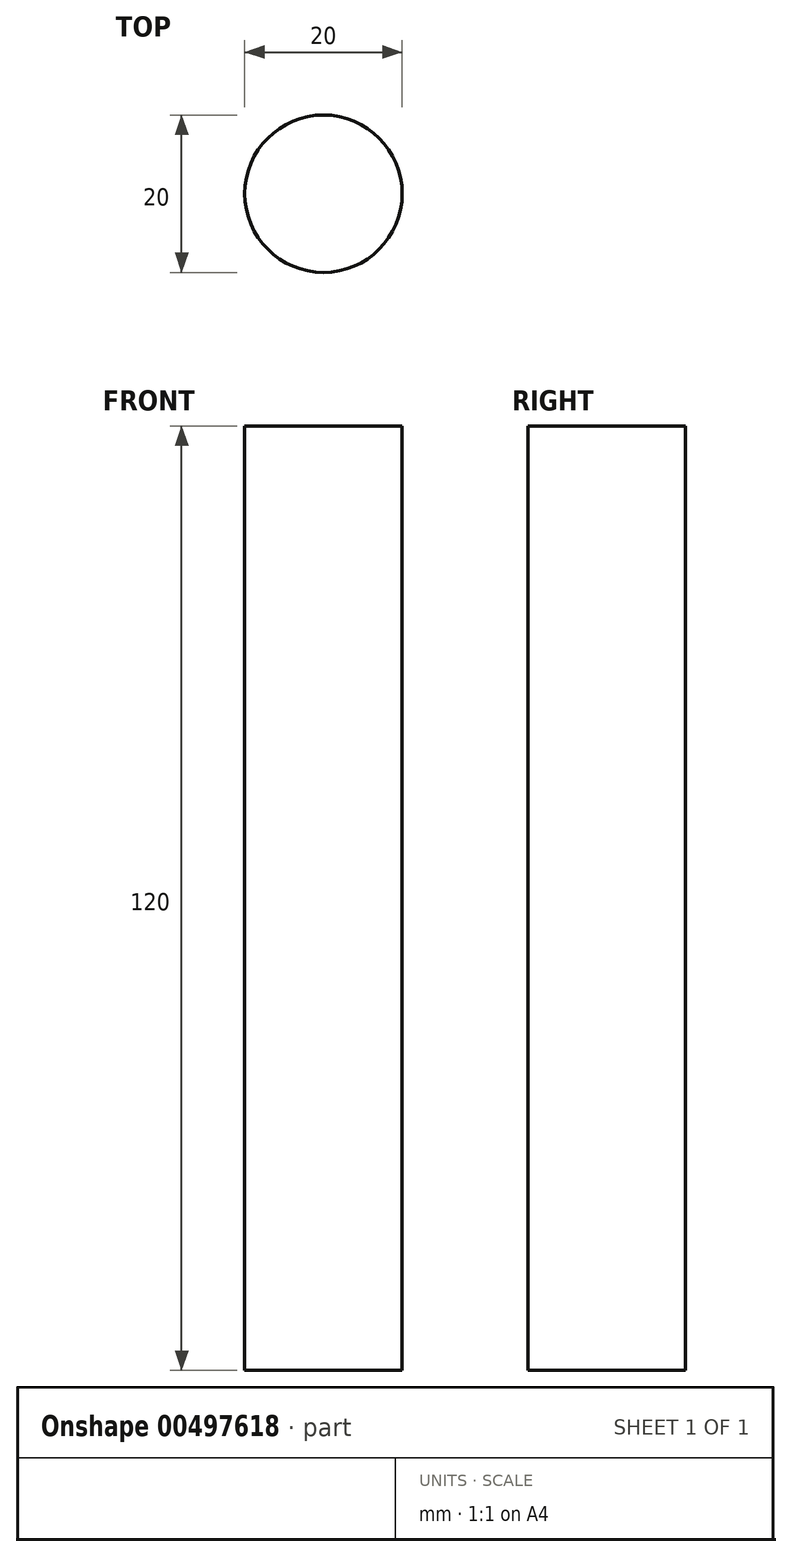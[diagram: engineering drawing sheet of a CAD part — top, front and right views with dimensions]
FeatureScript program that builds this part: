
annotation { "Feature Type Name" : "Feature", "Feature Type Description" : "" }
export const myFeature = defineFeature(function(context is Context, id is Id, definition is map)
    precondition{}
    {
        {
            var Q0;
            Q0=qCreatedBy(makeId("Top.planeOp"),FACE);
            var sketch = newSketch(context, id + "F0", { "sketchPlane" : qUnion([Q0])});
            skCircle(sketch, "E0", {"center": v(0, 0) * mm, "radius": 10 * mm});
            skSolve(sketch);
        }
        {
            var Q0;
            Q0 = qSketchRegion(id + "F0", true);
            extrude(context, id + "F1", {"entities" : qUnion([Q0]), "depth" : 120 * mm, "offsetDistance" : 25 * mm});
        }
    });
